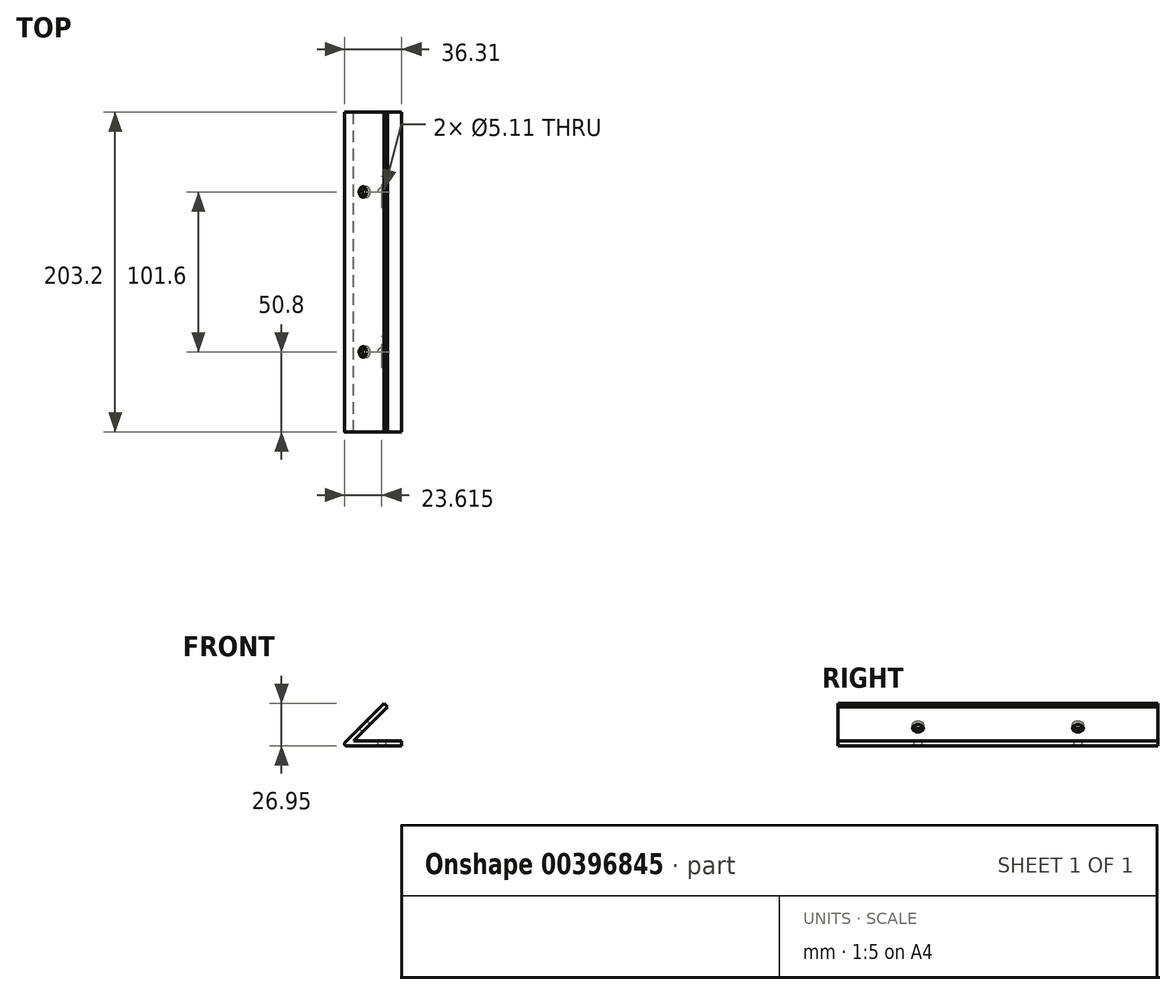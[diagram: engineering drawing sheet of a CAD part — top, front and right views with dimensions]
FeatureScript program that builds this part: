
annotation { "Feature Type Name" : "Feature", "Feature Type Description" : "" }
export const myFeature = defineFeature(function(context is Context, id is Id, definition is map)
    precondition{}
    {
        {
            var Q0;
            Q0=qCreatedBy(makeId("Front.planeOp"),FACE);
            var sketch = newSketch(context, id + "F0", { "sketchPlane" : qUnion([Q0])});
            skLineSegment(sketch, "E0", {"start": v(0, 0) * mm, "end": v(21.52, 21.52) * mm});
            skLineSegment(sketch, "E1", {"start": v(21.52, 21.52) * mm, "end": v(19.28, 23.77) * mm});
            skLineSegment(sketch, "E2", {"start": v(19.28, 23.77) * mm, "end": v(-7.67, -3.18) * mm});
            skLineSegment(sketch, "E3", {"start": v(-7.67, -3.18) * mm, "end": v(30.43, -3.18) * mm});
            skLineSegment(sketch, "E4", {"start": v(30.43, -3.18) * mm, "end": v(30.43, 0) * mm});
            skLineSegment(sketch, "E5", {"start": v(30.43, 0) * mm, "end": v(0, 0) * mm});
            skSolve(sketch);
        }
        {
            var Q0;
            Q0=makeQuery(id+"F0.imprint","IMPRINT",FACE,{"disambiguationData":[TD([[makeQuery(id+"F0.imprint","IMPRINT",EDGE,{"derivedFrom":sQuery(id+"F0.wireOp",EDGE,"E0")}),1.0]])]});
            extrude(context, id + "F1", {"entities" : qUnion([Q0]), "depth" : 203.2 * mm});
        }
        {
            var Q0;
            Q0=makeQuery(id+"F1.opExtrude","SWEPT_FACE",FACE,{"disambiguationData":[OSD([sQuery(id+"F0.wireOp",EDGE,"E2")])]});
            var sketch = newSketch(context, id + "F2", { "sketchPlane" : qUnion([Q0])});
            skCircle(sketch, "E6", {"center": v(50.8, 11.38) * mm, "radius": 3.38 * mm});
            skCircle(sketch, "E7", {"center": v(152.4, 11.38) * mm, "radius": 3.38 * mm});
            skSolve(sketch);
        }
        {
            var Q0;
            Q0 = qSketchRegion(id + "F2", true);
            var Q1;
            Q1=makeQuery(id+"F1.opExtrude","SWEPT_FACE",FACE,{"disambiguationData":[OSD([sQuery(id+"F0.wireOp",EDGE,"E0")])]});
            extrude(context, id + "F3", {"entities" : qUnion([Q0]), "operationType" : NewBodyOperationType.REMOVE, "endBound" : BoundingType.UP_TO_SURFACE, "oppositeDirection" : true, "endBoundEntityFace" : qUnion([Q1]), "depth" : 25.4 * mm});
        }
        {
            var Q0;
            Q0=makeQuery(id+"F1.opExtrude","SWEPT_FACE",FACE,{"disambiguationData":[OSD([sQuery(id+"F0.wireOp",EDGE,"E3")])]});
            var sketch = newSketch(context, id + "F4", { "sketchPlane" : qUnion([Q0])});
            skCircle(sketch, "E8", {"center": v(17.73, 152.4) * mm, "radius": 2.55 * mm});
            skCircle(sketch, "E9", {"center": v(17.73, 50.8) * mm, "radius": 2.55 * mm});
            skSolve(sketch);
        }
        {
            var Q0;
            Q0 = qSketchRegion(id + "F4", true);
            var Q1;
            Q1=makeQuery(id+"F1.opExtrude","SWEPT_FACE",FACE,{"disambiguationData":[OSD([sQuery(id+"F0.wireOp",EDGE,"E5")])]});
            extrude(context, id + "F5", {"entities" : qUnion([Q0]), "operationType" : NewBodyOperationType.REMOVE, "endBound" : BoundingType.UP_TO_SURFACE, "oppositeDirection" : true, "endBoundEntityFace" : qUnion([Q1]), "depth" : 25.4 * mm});
        }
        {
            var Q0;
            Q0=makeQuery(id+"F1.opExtrude","SWEPT_EDGE",EDGE,{"disambiguationData":[OSD([sQuery(id+"F0.wireOp",EDGE,"E2"),sQuery(id+"F0.wireOp",EDGE,"E3")])]});
            fillet(context, id + "F6", {"entities" : qUnion([Q0]), "radius" : 1.26 * mm, "tangentPropagation" : true, "allowEdgeOverflow" : false});
        }
    });
